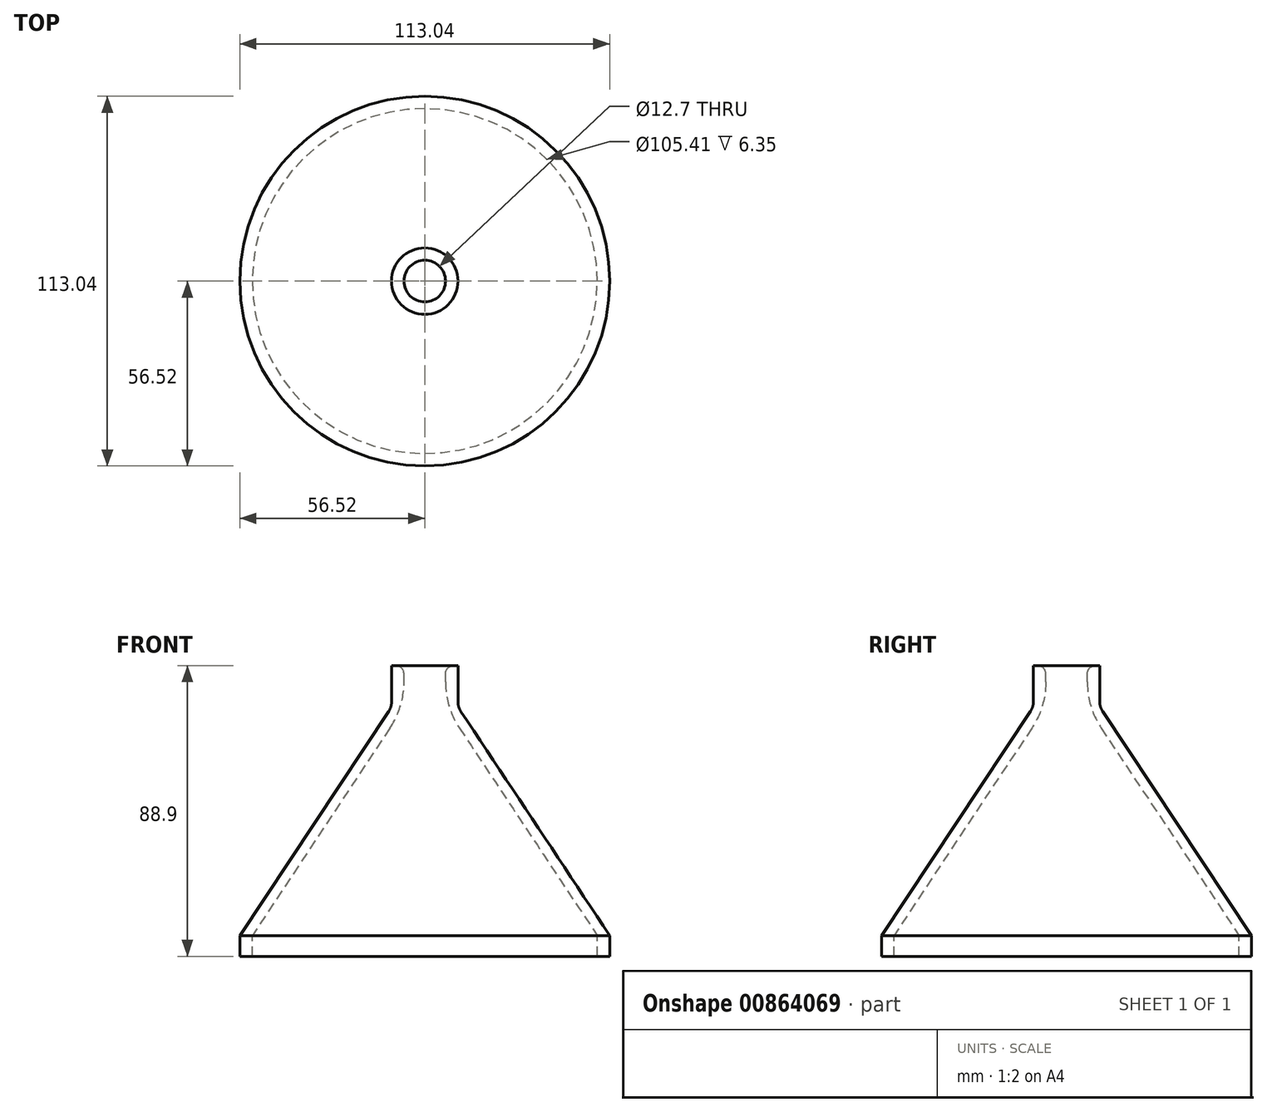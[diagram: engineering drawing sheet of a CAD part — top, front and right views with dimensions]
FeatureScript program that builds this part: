
annotation { "Feature Type Name" : "Feature", "Feature Type Description" : "" }
export const myFeature = defineFeature(function(context is Context, id is Id, definition is map)
    precondition{}
    {
        {
            var Q0;
            Q0=qCreatedBy(makeId("Front.planeOp"),FACE);
            var sketch = newSketch(context, id + "F0", { "sketchPlane" : qUnion([Q0])});
            skLineSegment(sketch, "E0", {"start": v(52.7, 0) * mm, "end": v(52.7, 6.35) * mm});
            skLineSegment(sketch, "E1", {"start": v(56.51, 0) * mm, "end": v(56.51, 6.35) * mm});
            skLineSegment(sketch, "E2", {"start": v(52.7, 0) * mm, "end": v(56.51, 0) * mm});
            skPoint(sketch, "E3", {"position": v(6.35, 76.2) * mm});
            skLineSegment(sketch, "E4", {"start": v(10.16, 76.2) * mm, "end": v(10.16, 88.9) * mm});
            skLineSegment(sketch, "E5", {"start": v(6.35, 76.2) * mm, "end": v(6.35, 88.9) * mm});
            skLineSegment(sketch, "E6", {"start": v(6.35, 88.9) * mm, "end": v(6.35, 88.9) * mm});
            skLineSegment(sketch, "E7", {"start": v(10.16, 88.9) * mm, "end": v(6.35, 88.9) * mm});
            skLineSegment(sketch, "E8", {"start": v(10.16, 76.2) * mm, "end": v(56.51, 6.35) * mm});
            skLineSegment(sketch, "E9", {"start": v(52.7, 6.35) * mm, "end": v(6.35, 76.2) * mm});
            skSolve(sketch);
        }
        {
            var Q0;
            Q0=qCreatedBy(makeId("Front.planeOp"),FACE);
            var sketch = newSketch(context, id + "F1", { "sketchPlane" : qUnion([Q0])});
            skLineSegment(sketch, "E10", {"start": v(0, 206.58) * mm, "end": v(0, -123.7) * mm});
            skSolve(sketch);
        }
        {
            var Q0;
            Q0=makeQuery(id+"F0.imprint","IMPRINT",FACE,{"disambiguationData":[TD([[makeQuery(id+"F0.imprint","IMPRINT",EDGE,{"derivedFrom":sQuery(id+"F0.wireOp",EDGE,"E0")}),-1.0]])]});
            var Q1;
            Q1=sQuery(id+"F1.wireOp",EDGE,"E10");
            revolve(context, id + "F2", {"surfaceOperationType" : NewSurfaceOperationType.NEW, "entities" : qUnion([Q0]), "axis" : qUnion([Q1]), "revolveType" : RevolveType.FULL});
        }
        {
            var Q0;
            Q0=makeQuery(id+"F2.opRevolve","SWEPT_EDGE",EDGE,{"disambiguationData":[OSD([sQuery(id+"F0.wireOp",EDGE,"E4"),sQuery(id+"F0.wireOp",EDGE,"E8")])]});
            fillet(context, id + "F3", {"entities" : qUnion([Q0]), "radius" : 5.08 * mm, "tangentPropagation" : true, "allowEdgeOverflow" : false});
        }
        {
            var Q0;
            Q0=makeQuery(id+"F2.opRevolve","SWEPT_EDGE",EDGE,{"disambiguationData":[OSD([sQuery(id+"F0.wireOp",EDGE,"E5"),sQuery(id+"F0.wireOp",EDGE,"E9")])]});
            fillet(context, id + "F4", {"entities" : qUnion([Q0]), "radius" : 25.4 * mm, "tangentPropagation" : true, "allowEdgeOverflow" : false});
        }
        {
            var Q0;
            Q0=makeQuery(id+"F2.opRevolve","SWEPT_EDGE",EDGE,{"disambiguationData":[OSD([sQuery(id+"F0.wireOp",EDGE,"E5"),sQuery(id+"F0.wireOp",EDGE,"E7")])]});
            fillet(context, id + "F5", {"entities" : qUnion([Q0]), "radius" : 2.54 * mm, "tangentPropagation" : true, "allowEdgeOverflow" : false});
        }
    });
